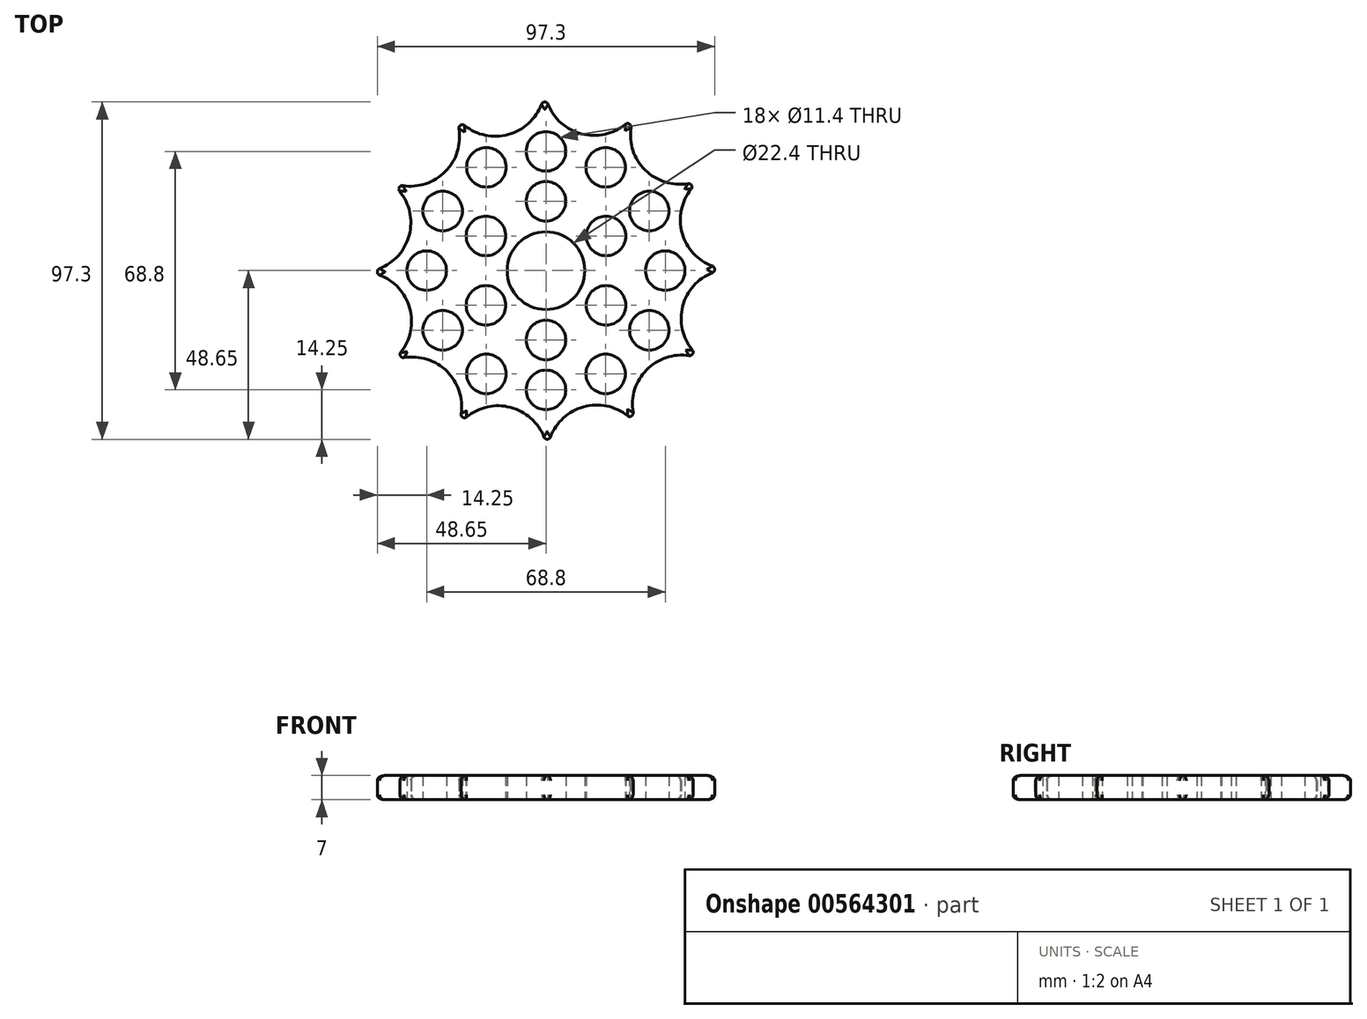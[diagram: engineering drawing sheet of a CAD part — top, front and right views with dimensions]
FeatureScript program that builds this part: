
annotation { "Feature Type Name" : "Feature", "Feature Type Description" : "" }
export const myFeature = defineFeature(function(context is Context, id is Id, definition is map)
    precondition{}
    {
        {
            var Q0;
            Q0=qCreatedBy(makeId("Top.planeOp"),FACE);
            var sketch = newSketch(context, id + "F0", { "sketchPlane" : qUnion([Q0])});
            skCircle(sketch, "E0", {"center": v(0, 0) * mm, "radius": 11.2 * mm});
            skCircle(sketch, "E1", {"center": v(0, 20) * mm, "radius": 5.7 * mm});
            skCircle(sketch, "E2", {"center": v(0, 34.4) * mm, "radius": 5.7 * mm});
            skArc(sketch, "E3", {"start": v(-27.76, 47.48) * mm, "mid": v(-27.85, 47.43) * mm, "end": v(-27.95, 47.37) * mm});
            skArc(sketch, "E4", {"start": v(-0.3, 55) * mm, "mid": v(10.26, 39.44) * mm, "end": v(27.05, 47.89) * mm});
            skArc(sketch, "E5.1.0", {"start": v(-27.76, 47.48) * mm, "mid": v(-10.84, 39.28) * mm, "end": v(-0.52, 55) * mm});
            skArc(sketch, "E5.2.0", {"start": v(-47.78, 27.24) * mm, "mid": v(-29.03, 28.6) * mm, "end": v(-27.95, 47.37) * mm});
            skArc(sketch, "E5.3.0", {"start": v(-55, -0.3) * mm, "mid": v(-39.44, 10.26) * mm, "end": v(-47.89, 27.05) * mm});
            skArc(sketch, "E5.4.0", {"start": v(-47.48, -27.76) * mm, "mid": v(-39.28, -10.84) * mm, "end": v(-55, -0.52) * mm});
            skArc(sketch, "E5.5.0", {"start": v(-27.24, -47.78) * mm, "mid": v(-28.6, -29.03) * mm, "end": v(-47.37, -27.95) * mm});
            skArc(sketch, "E5.6.0", {"start": v(0.4, -53.78) * mm, "mid": v(-10.85, -39.3) * mm, "end": v(-27.05, -47.89) * mm});
            skArc(sketch, "E5.7.0", {"start": v(27.76, -47.48) * mm, "mid": v(10.84, -39.28) * mm, "end": v(0.52, -55) * mm});
            skArc(sketch, "E5.8.0", {"start": v(47.78, -27.24) * mm, "mid": v(29.03, -28.6) * mm, "end": v(27.95, -47.37) * mm});
            skArc(sketch, "E5.9.0", {"start": v(55, 0.3) * mm, "mid": v(39.44, -10.26) * mm, "end": v(47.89, -27.05) * mm});
            skArc(sketch, "E5.10.0", {"start": v(47.48, 27.76) * mm, "mid": v(39.28, 10.84) * mm, "end": v(55, 0.52) * mm});
            skArc(sketch, "E5.11.0", {"start": v(27.24, 47.78) * mm, "mid": v(28.6, 29.03) * mm, "end": v(47.37, 27.95) * mm});
            skCircle(sketch, "E6.1.0", {"center": v(-17.2, 29.8) * mm, "radius": 5.7 * mm});
            skCircle(sketch, "E6.2.0", {"center": v(-29.8, 17.2) * mm, "radius": 5.7 * mm});
            skCircle(sketch, "E6.3.0", {"center": v(-34.4, 0) * mm, "radius": 5.7 * mm});
            skCircle(sketch, "E6.4.0", {"center": v(-29.8, -17.2) * mm, "radius": 5.7 * mm});
            skCircle(sketch, "E6.5.0", {"center": v(-17.2, -29.8) * mm, "radius": 5.7 * mm});
            skCircle(sketch, "E6.6.0", {"center": v(0, -34.4) * mm, "radius": 5.7 * mm});
            skCircle(sketch, "E6.7.0", {"center": v(17.2, -29.8) * mm, "radius": 5.7 * mm});
            skCircle(sketch, "E6.8.0", {"center": v(29.8, -17.2) * mm, "radius": 5.7 * mm});
            skCircle(sketch, "E6.9.0", {"center": v(34.4, 0) * mm, "radius": 5.7 * mm});
            skCircle(sketch, "E6.10.0", {"center": v(29.8, 17.2) * mm, "radius": 5.7 * mm});
            skCircle(sketch, "E6.11.0", {"center": v(17.2, 29.8) * mm, "radius": 5.7 * mm});
            skCircle(sketch, "E7.1.0", {"center": v(-17.32, 10) * mm, "radius": 5.7 * mm});
            skCircle(sketch, "E7.2.0", {"center": v(-17.32, -10) * mm, "radius": 5.7 * mm});
            skCircle(sketch, "E7.3.0", {"center": v(0, -20) * mm, "radius": 5.7 * mm});
            skCircle(sketch, "E7.4.0", {"center": v(17.32, -10) * mm, "radius": 5.7 * mm});
            skCircle(sketch, "E7.5.0", {"center": v(17.32, 10) * mm, "radius": 5.7 * mm});
            skArc(sketch, "E8.trimOffspring", {"start": v(-47.78, 27.24) * mm, "mid": v(-47.83, 27.15) * mm, "end": v(-47.89, 27.05) * mm});
            skArc(sketch, "E9.trimOffspring", {"start": v(-47.48, -27.76) * mm, "mid": v(-47.43, -27.85) * mm, "end": v(-47.37, -27.95) * mm});
            skArc(sketch, "E10.trimOffspring", {"start": v(-27.24, -47.78) * mm, "mid": v(-27.15, -47.83) * mm, "end": v(-27.05, -47.89) * mm});
            skArc(sketch, "E11.trimOffspring", {"start": v(27.76, -47.48) * mm, "mid": v(27.85, -47.43) * mm, "end": v(27.95, -47.37) * mm});
            skArc(sketch, "E12.trimOffspring", {"start": v(47.78, -27.24) * mm, "mid": v(47.83, -27.15) * mm, "end": v(47.89, -27.05) * mm});
            skArc(sketch, "E13.trimOffspring", {"start": v(55, 0.3) * mm, "mid": v(55, 0.4) * mm, "end": v(55, 0.52) * mm});
            skArc(sketch, "E14.trimOffspring", {"start": v(47.48, 27.76) * mm, "mid": v(47.43, 27.85) * mm, "end": v(47.37, 27.95) * mm});
            skArc(sketch, "E15.trimOffspring", {"start": v(27.24, 47.78) * mm, "mid": v(27.15, 47.83) * mm, "end": v(27.05, 47.89) * mm});
            skArc(sketch, "E16.trimOffspring", {"start": v(-0.3, 55) * mm, "mid": v(-0.4, 55) * mm, "end": v(-0.52, 55) * mm});
            skSolve(sketch);
        }
        {
            var Q0;
            Q0=makeQuery(id+"F0.imprint","IMPRINT",FACE,{"disambiguationData":[TD([[makeQuery(id+"F0.imprint","IMPRINT",EDGE,{"derivedFrom":sQuery(id+"F0.wireOp",EDGE,"E0")}),-1.0]])]});
            extrude(context, id + "F1", {"entities" : qUnion([Q0]), "depth" : 7 * mm, "offsetDistance" : 25 * mm});
        }
        {
            var Q0;
            Q0=makeQuery(id+"F1.opExtrude","SWEPT_EDGE",EDGE,{"disambiguationData":[OSD([sQuery(id+"F0.wireOp",EDGE,"E5.7.0"),sQuery(id+"F0.wireOp",EDGE,"E5.8.0")])]});
            var Q1;
            Q1=makeQuery(id+"F1.opExtrude","SWEPT_EDGE",EDGE,{"disambiguationData":[OSD([sQuery(id+"F0.wireOp",EDGE,"E5.8.0"),sQuery(id+"F0.wireOp",EDGE,"E5.9.0")])]});
            var Q2;
            Q2=makeQuery(id+"F1.opExtrude","SWEPT_EDGE",EDGE,{"disambiguationData":[OSD([sQuery(id+"F0.wireOp",EDGE,"E5.9.0"),sQuery(id+"F0.wireOp",EDGE,"E5.10.0")])]});
            var Q3;
            Q3=makeQuery(id+"F1.opExtrude","SWEPT_EDGE",EDGE,{"disambiguationData":[OSD([sQuery(id+"F0.wireOp",EDGE,"E5.10.0"),sQuery(id+"F0.wireOp",EDGE,"E5.11.0")])]});
            var Q4;
            Q4=makeQuery(id+"F1.opExtrude","SWEPT_EDGE",EDGE,{"disambiguationData":[OSD([sQuery(id+"F0.wireOp",EDGE,"E5.6.0"),sQuery(id+"F0.wireOp",EDGE,"E5.7.0")])]});
            var Q5;
            Q5=makeQuery(id+"F1.opExtrude","SWEPT_EDGE",EDGE,{"disambiguationData":[OSD([sQuery(id+"F0.wireOp",EDGE,"E5.5.0"),sQuery(id+"F0.wireOp",EDGE,"E5.6.0")])]});
            var Q6;
            Q6=makeQuery(id+"F1.opExtrude","SWEPT_EDGE",EDGE,{"disambiguationData":[OSD([sQuery(id+"F0.wireOp",EDGE,"E5.4.0"),sQuery(id+"F0.wireOp",EDGE,"E5.5.0")])]});
            var Q7;
            Q7=makeQuery(id+"F1.opExtrude","SWEPT_EDGE",EDGE,{"disambiguationData":[OSD([sQuery(id+"F0.wireOp",EDGE,"E5.3.0"),sQuery(id+"F0.wireOp",EDGE,"E5.4.0")])]});
            var Q8;
            Q8=makeQuery(id+"F1.opExtrude","SWEPT_EDGE",EDGE,{"disambiguationData":[OSD([sQuery(id+"F0.wireOp",EDGE,"E5.2.0"),sQuery(id+"F0.wireOp",EDGE,"E5.3.0")])]});
            var Q9;
            Q9=makeQuery(id+"F1.opExtrude","SWEPT_EDGE",EDGE,{"disambiguationData":[OSD([sQuery(id+"F0.wireOp",EDGE,"E5.1.0"),sQuery(id+"F0.wireOp",EDGE,"E5.2.0")])]});
            var Q10;
            Q10=makeQuery(id+"F1.opExtrude","SWEPT_EDGE",EDGE,{"disambiguationData":[OSD([sQuery(id+"F0.wireOp",EDGE,"E4"),sQuery(id+"F0.wireOp",EDGE,"E5.1.0")])]});
            var Q11;
            Q11=makeQuery(id+"F1.opExtrude","SWEPT_EDGE",EDGE,{"disambiguationData":[OSD([sQuery(id+"F0.wireOp",EDGE,"E4"),sQuery(id+"F0.wireOp",EDGE,"E5.11.0")])]});
            fillet(context, id + "F2", {"entities" : qUnion([Q0, Q1, Q2, Q3, Q4, Q5, Q6, Q7, Q8, Q9, Q10, Q11]), "radius" : 1 * mm, "tangentPropagation" : true, "allowEdgeOverflow" : false});
        }
        {
            var Q0;
            Q0=makeQuery(id+"F1.opExtrude","CAP_EDGE",EDGE,{"disambiguationData":[OSD([sQuery(id+"F0.wireOp",EDGE,"E5.6.0")])],"isStart":false});
            var Q1;
            Q1=makeQuery(id+"F1.opExtrude","CAP_EDGE",EDGE,{"disambiguationData":[OSD([sQuery(id+"F0.wireOp",EDGE,"E5.5.0")])],"isStart":true});
            fillet(context, id + "F3", {"entities" : qUnion([Q0, Q1]), "radius" : 1.5 * mm, "tangentPropagation" : true, "allowEdgeOverflow" : false});
        }
    });
